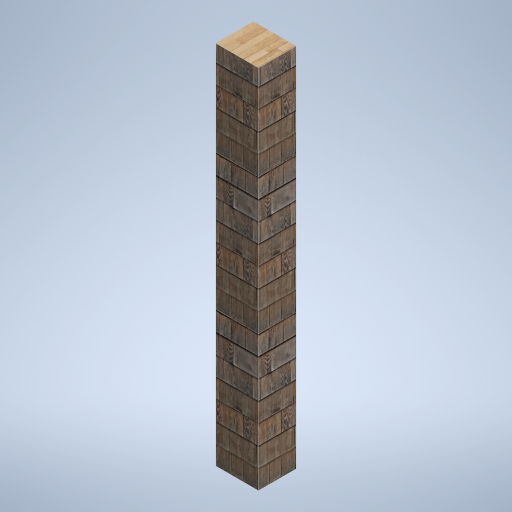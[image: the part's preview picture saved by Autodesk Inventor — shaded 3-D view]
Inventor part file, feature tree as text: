
AUTODESK INVENTOR PART (.ipt)
format: ipt  version: 2024.2 (Build 282272000, 272)  size: 344,064 bytes
history: native  units: in
note: dims shown in document units (in); Inventor stores cm internally (conversion verified against a paired STEP export)
features: other x3, sketch x1
ambient origin geometry x8: Origin, YZ Plane, XZ Plane, XY Plane, X Axis, Y Axis, Z Axis, Center Point
bodies: Solid1 (feature_tree)
feature tree (4):
  other  "support_column_01.ipt"
  other  "Solid1::support_column_01.ipt"
  other  "TaggingFeature1"
  sketch  "Sketch1"  dims[d0=0.3937in]
